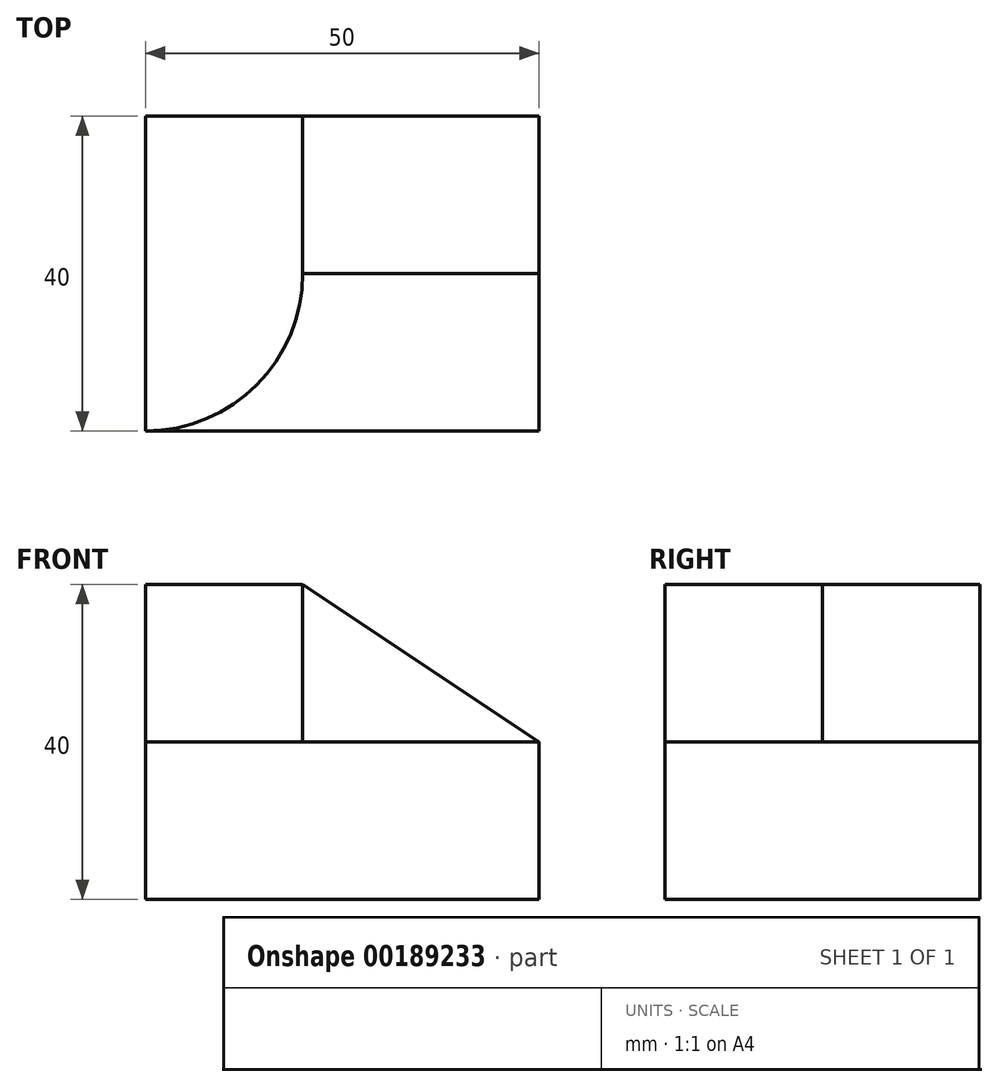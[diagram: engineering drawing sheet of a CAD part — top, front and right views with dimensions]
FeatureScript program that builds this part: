
annotation { "Feature Type Name" : "Feature", "Feature Type Description" : "" }
export const myFeature = defineFeature(function(context is Context, id is Id, definition is map)
    precondition{}
    {
        {
            var Q0;
            Q0=qCreatedBy(makeId("Top.planeOp"),FACE);
            var sketch = newSketch(context, id + "F0", { "sketchPlane" : qUnion([Q0])});
            skLineSegment(sketch, "E0.bottom", {"start": v(0, 0) * mm, "end": v(50, 0) * mm});
            skLineSegment(sketch, "E0.top", {"start": v(0, 40) * mm, "end": v(50, 40) * mm});
            skLineSegment(sketch, "E0.left", {"start": v(0, 0) * mm, "end": v(0, 40) * mm});
            skLineSegment(sketch, "E0.right", {"start": v(50, 0) * mm, "end": v(50, 40) * mm});
            skSolve(sketch);
        }
        {
            var Q0;
            Q0=makeQuery(id+"F0.imprint","IMPRINT",FACE,{"disambiguationData":[TD([[makeQuery(id+"F0.imprint","IMPRINT",EDGE,{"derivedFrom":sQuery(id+"F0.wireOp",EDGE,"E0.bottom")}),1.0]])]});
            extrude(context, id + "F1", {"entities" : qUnion([Q0]), "depth" : 20 * mm});
        }
        {
            var Q0;
            Q0=makeQuery(id+"F1.opExtrude","CAP_FACE",FACE,{"disambiguationData":[OSD([sQuery(id+"F0.wireOp",EDGE,"E0.bottom"),sQuery(id+"F0.wireOp",EDGE,"E0.top"),sQuery(id+"F0.wireOp",EDGE,"E0.left"),sQuery(id+"F0.wireOp",EDGE,"E0.right")])],"isStart":false});
            var sketch = newSketch(context, id + "F2", { "sketchPlane" : qUnion([Q0])});
            skLineSegment(sketch, "E1.0", {"start": v(0, 0) * mm, "end": v(0, 40) * mm});
            skLineSegment(sketch, "E2.0", {"start": v(0, 40) * mm, "end": v(20, 40) * mm});
            skLineSegment(sketch, "E3", {"start": v(20, 40) * mm, "end": v(20, 20) * mm});
            skArc(sketch, "E4", {"start": v(0, 0) * mm, "mid": v(14.14, 5.86) * mm, "end": v(20, 20) * mm});
            skPoint(sketch, "E5.orphan", {"position": v(50, 40) * mm});
            skSolve(sketch);
        }
        {
            var Q0;
            Q0=makeQuery(id+"F2.imprint","IMPRINT",FACE,{"disambiguationData":[TD([[makeQuery(id+"F2.imprint","IMPRINT",EDGE,{"derivedFrom":sQuery(id+"F2.wireOp",EDGE,"E1.0")}),-1.0]])]});
            extrude(context, id + "F3", {"entities" : qUnion([Q0]), "operationType" : NewBodyOperationType.ADD, "depth" : 20 * mm});
        }
        {
            var Q0;
            Q0=makeQuery(id+"F3.boolean.opBoolean","MERGE",FACE,{"derivedFrom":[makeQuery(id+"F1.opExtrude","SWEPT_FACE",FACE,{"disambiguationData":[OSD([sQuery(id+"F0.wireOp",EDGE,"E0.top")])]}),makeQuery(id+"F3.opExtrude","SWEPT_FACE",FACE,{"disambiguationData":[OSD([sQuery(id+"F2.wireOp",EDGE,"E2.0")])]})]});
            var sketch = newSketch(context, id + "F4", { "sketchPlane" : qUnion([Q0])});
            skLineSegment(sketch, "E6", {"start": v(-20, 40) * mm, "end": v(-50, 20) * mm});
            skLineSegment(sketch, "E7.0", {"start": v(-20, 40) * mm, "end": v(-20, 20) * mm});
            skLineSegment(sketch, "E8.0", {"start": v(-20, 20) * mm, "end": v(-50, 20) * mm});
            skSolve(sketch);
        }
        {
            var Q0;
            Q0=makeQuery(id+"F4.imprint","IMPRINT",FACE,{"disambiguationData":[TD([[makeQuery(id+"F4.imprint","IMPRINT",EDGE,{"derivedFrom":sQuery(id+"F4.wireOp",EDGE,"E6")}),1.0]])]});
            extrude(context, id + "F5", {"entities" : qUnion([Q0]), "operationType" : NewBodyOperationType.ADD, "oppositeDirection" : true, "depth" : 20 * mm});
        }
    });
